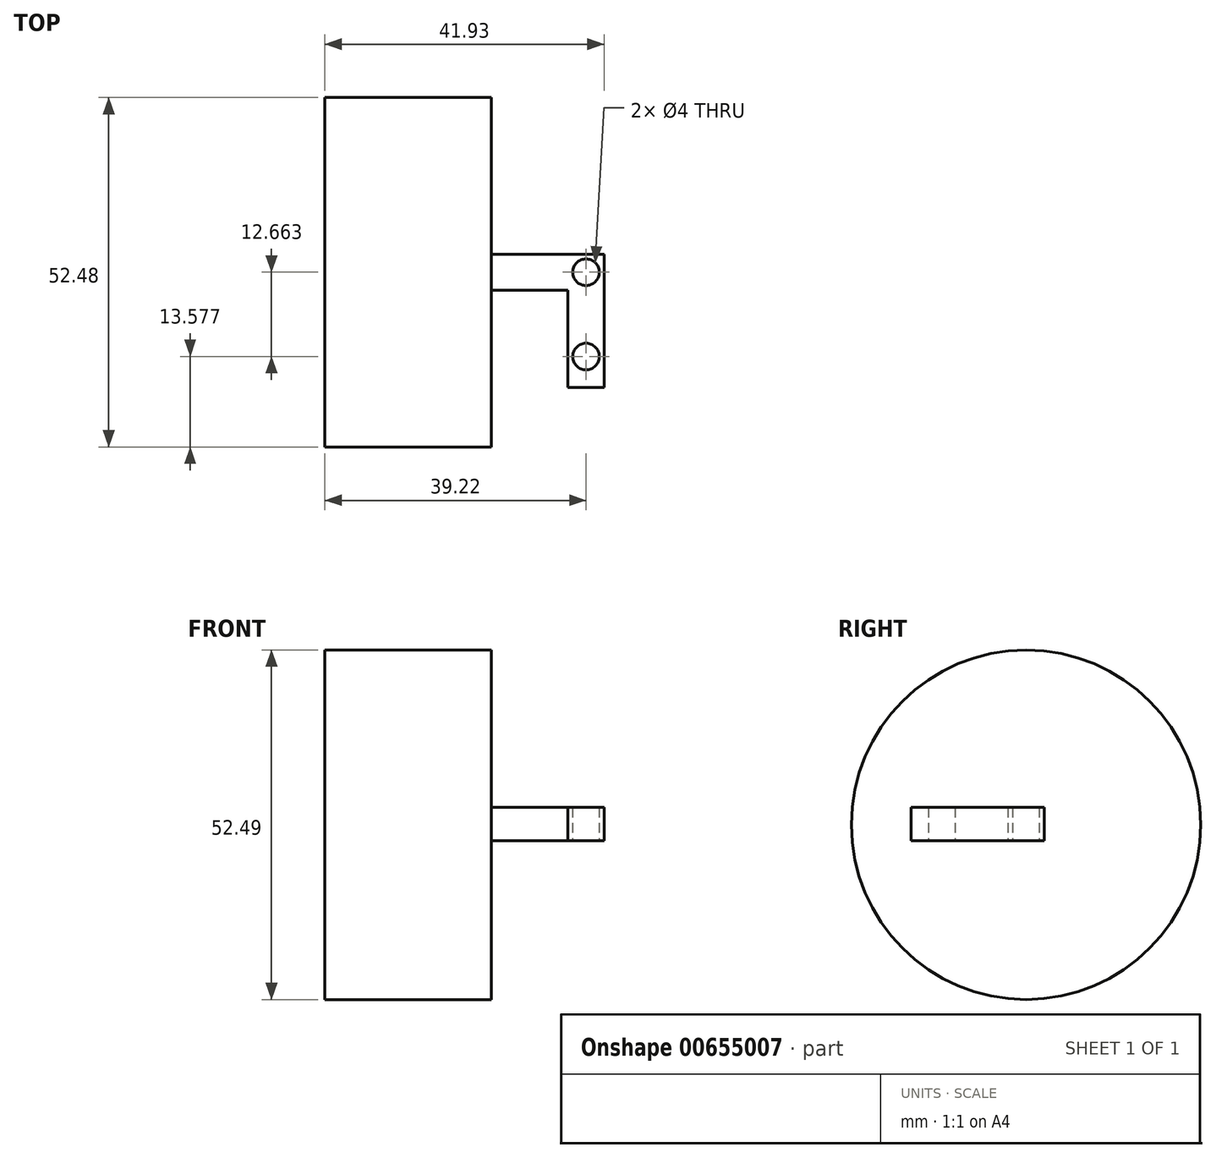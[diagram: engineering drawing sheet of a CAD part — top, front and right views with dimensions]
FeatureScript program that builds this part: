
annotation { "Feature Type Name" : "Feature", "Feature Type Description" : "" }
export const myFeature = defineFeature(function(context is Context, id is Id, definition is map)
    precondition{}
    {
        {
            var Q0;
            Q0=qCreatedBy(makeId("Top.planeOp"),FACE);
            var sketch = newSketch(context, id + "F0", { "sketchPlane" : qUnion([Q0])});
            skLineSegment(sketch, "E0.bottom", {"start": v(2.71, 10) * mm, "end": v(-2.71, 10) * mm});
            skLineSegment(sketch, "E0.top", {"start": v(2.71, -10) * mm, "end": v(-2.71, -10) * mm});
            skLineSegment(sketch, "E0.left", {"start": v(2.71, 10) * mm, "end": v(2.71, -10) * mm});
            skLineSegment(sketch, "E0.right", {"start": v(-2.71, 10) * mm, "end": v(-2.71, -10) * mm});
            skPoint(sketch, "E0.middle", {"position": v(0, 0) * mm});
            skLineSegment(sketch, "E1.bottom", {"start": v(-2.71, 10) * mm, "end": v(-14.22, 10) * mm});
            skLineSegment(sketch, "E1.top", {"start": v(-2.71, 4.56) * mm, "end": v(-14.22, 4.56) * mm});
            skLineSegment(sketch, "E1.left", {"start": v(-2.71, 10) * mm, "end": v(-2.71, 4.56) * mm});
            skLineSegment(sketch, "E1.right", {"start": v(-14.22, 10) * mm, "end": v(-14.22, 4.56) * mm});
            skCircle(sketch, "E2", {"center": v(0, 7.28) * mm, "radius": 2 * mm});
            skPoint(sketch, "E2.centerSnap0", {"position": v(-2.71, 7.28) * mm});
            skCircle(sketch, "E3", {"center": v(0, -5.38) * mm, "radius": 2 * mm});
            skSolve(sketch);
        }
        {
            var Q0;
            Q0=makeQuery(id+"F0.imprint","IMPRINT",FACE,{"disambiguationData":[TD([[makeQuery(id+"F0.imprint","IMPRINT",EDGE,{"derivedFrom":sQuery(id+"F0.wireOp",EDGE,"E1.bottom")}),1.0]])]});
            var Q1;
            Q1=makeQuery(id+"F0.imprint","IMPRINT",FACE,{"disambiguationData":[TD([[makeQuery(id+"F0.imprint","IMPRINT",EDGE,{"derivedFrom":sQuery(id+"F0.wireOp",EDGE,"E0.bottom")}),1.0]])]});
            extrude(context, id + "F1", {"entities" : qUnion([Q0, Q1]), "depth" : 5 * mm, "offsetDistance" : 25 * mm});
        }
        {
            var Q0;
            Q0=makeQuery(id+"F1.opExtrude","SWEPT_FACE",FACE,{"disambiguationData":[OSD([sQuery(id+"F0.wireOp",EDGE,"E1.right")])]});
            var sketch = newSketch(context, id + "F2", { "sketchPlane" : qUnion([Q0])});
            skCircle(sketch, "E4", {"center": v(-7.28, 2.4) * mm, "radius": 26.24 * mm});
            skPoint(sketch, "E4.centerSnap0", {"position": v(-7.28, 0) * mm});
            skSolve(sketch);
        }
        {
            var Q0;
            Q0=makeQuery(id+"F2.imprint","IMPRINT",FACE,{"disambiguationData":[TD([[makeQuery(id+"F2.imprint","IMPRINT",EDGE,{"derivedFrom":sQuery(id+"F2.wireOp",EDGE,"E4")}),1.0]])]});
            var Q1;
            {var subQ0=sQuery(id+"F0.wireOp",EDGE,"E1.right");Q1=makeQuery(id+"F2.imprint","IMPRINT",FACE,{"disambiguationData":[TD([[makeQuery(id+"F2.imprint","IMPRINT",EDGE,{"derivedFrom":makeQuery(id+"F1.opExtrude","CAP_EDGE",EDGE,{"disambiguationData":[OSD([subQ0])],"isStart":true})}),1.0]])]});}
            extrude(context, id + "F3", {"entities" : qUnion([Q0, Q1]), "operationType" : NewBodyOperationType.ADD, "depth" : 25 * mm, "offsetDistance" : 25 * mm});
        }
    });
